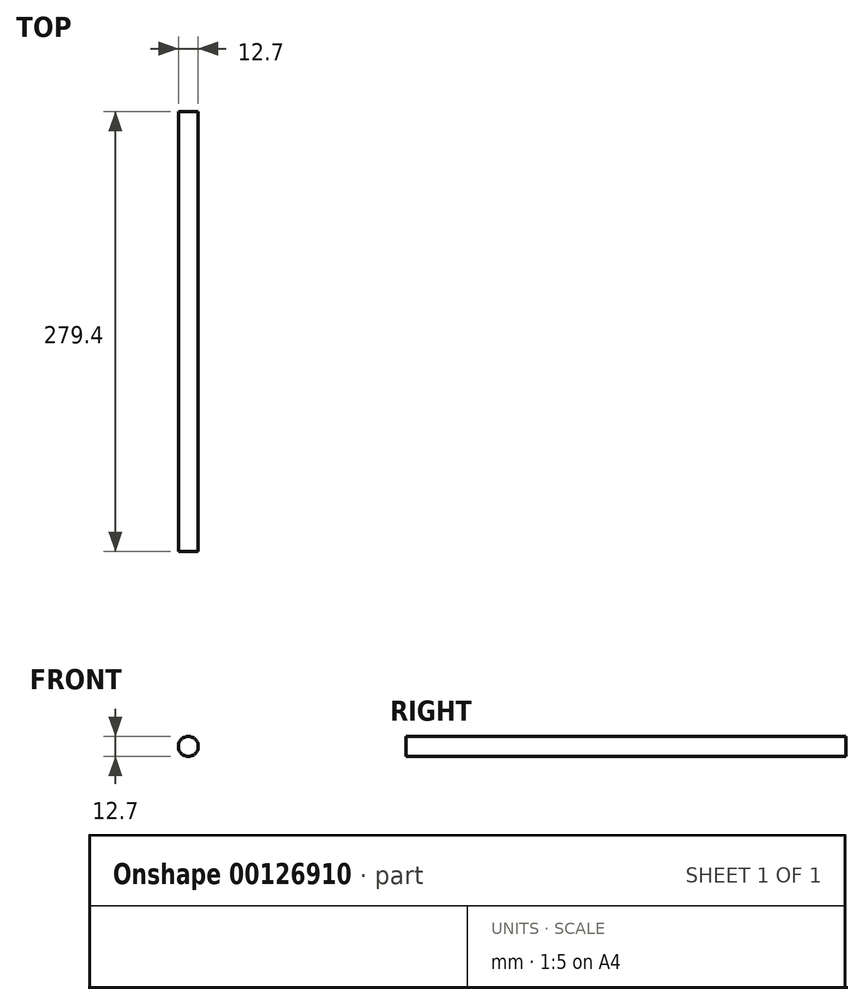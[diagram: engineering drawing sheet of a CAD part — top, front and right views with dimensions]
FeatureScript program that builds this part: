
annotation { "Feature Type Name" : "Feature", "Feature Type Description" : "" }
export const myFeature = defineFeature(function(context is Context, id is Id, definition is map)
    precondition{}
    {
        {
            var Q0;
            Q0=qCreatedBy(makeId("Front.planeOp"),FACE);
            var sketch = newSketch(context, id + "F0", { "sketchPlane" : qUnion([Q0])});
            skCircle(sketch, "E0", {"center": v(0, 0) * mm, "radius": 6.35 * mm});
            skSolve(sketch);
        }
        {
            var Q0;
            Q0 = qSketchRegion(id + "F0", true);
            extrude(context, id + "F1", {"entities" : qUnion([Q0]), "endBound" : BoundingType.SYMMETRIC, "depth" : 279.4 * mm});
        }
    });
